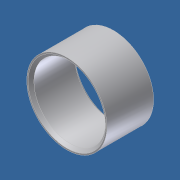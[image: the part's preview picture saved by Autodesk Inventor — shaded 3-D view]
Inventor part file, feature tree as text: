
AUTODESK INVENTOR PART (.ipt)
format: ipt  version: unknown  size: 177,152 bytes
history: native  units: in
note: dims shown in document units (in); Inventor stores cm internally (conversion verified against a paired STEP export)
features: extrude x1, chamfer x1, sketch x1
ambient origin geometry x8: Origin, YZ Plane, XZ Plane, XY Plane, X Axis, Y Axis, Z Axis, Center Point
bodies: Solid1 (feature_tree)
feature tree (3):
  extrude  "Extrusion1"  Depth=1.25in
  chamfer  "Chamfer1"  Distance=0.815in
  sketch  "Sketch1"  dims[d0=0.075in d1=1.25in d2=0.815in d3=0.0in d4=0.05in d5=0.125in d6=45.0deg]
